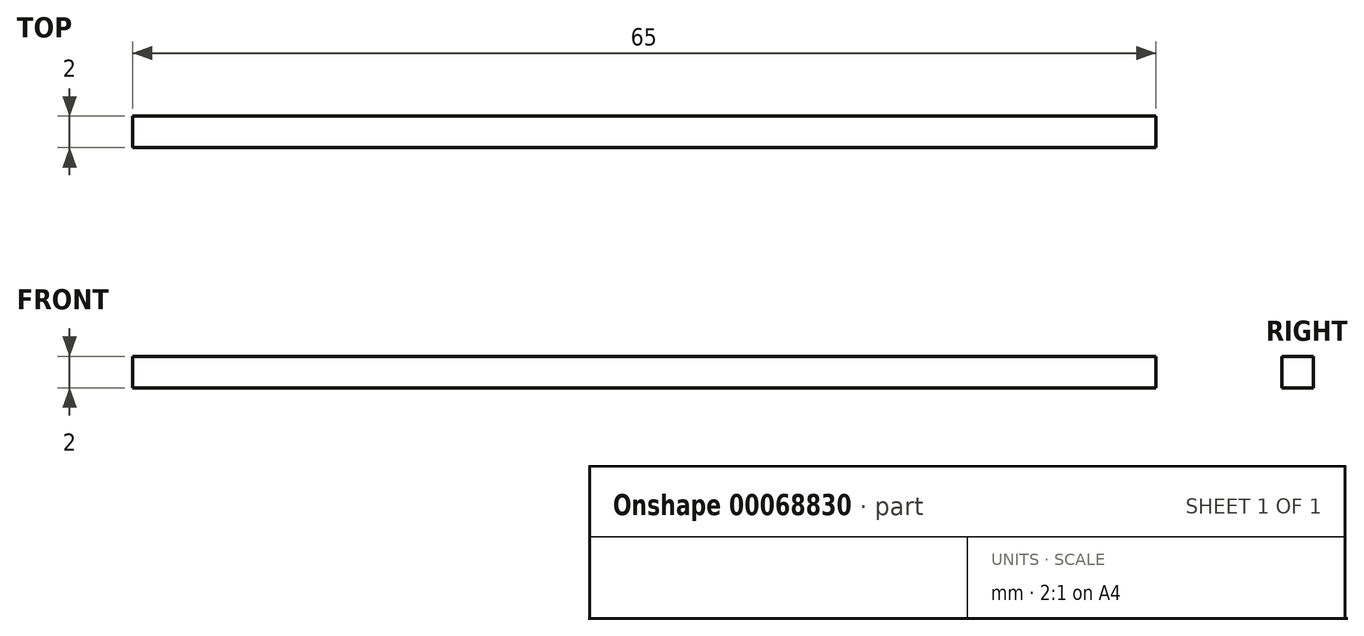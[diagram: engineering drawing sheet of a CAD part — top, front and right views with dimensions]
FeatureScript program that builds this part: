
annotation { "Feature Type Name" : "Feature", "Feature Type Description" : "" }
export const myFeature = defineFeature(function(context is Context, id is Id, definition is map)
    precondition{}
    {
        {
            var Q0;
            Q0=qCreatedBy(makeId("Top.planeOp"),FACE);
            var sketch = newSketch(context, id + "F0", { "sketchPlane" : qUnion([Q0])});
            skLineSegment(sketch, "E0.bottom", {"start": v(0, 0) * mm, "end": v(65, 0) * mm});
            skLineSegment(sketch, "E0.top", {"start": v(0, 2) * mm, "end": v(65, 2) * mm});
            skLineSegment(sketch, "E0.left", {"start": v(0, 0) * mm, "end": v(0, 2) * mm});
            skLineSegment(sketch, "E0.right", {"start": v(65, 0) * mm, "end": v(65, 2) * mm});
            skSolve(sketch);
        }
        {
            var Q0;
            Q0 = qSketchRegion(id + "F0", true);
            extrude(context, id + "F1", {"entities" : qUnion([Q0]), "depth" : 2 * mm});
        }
    });
